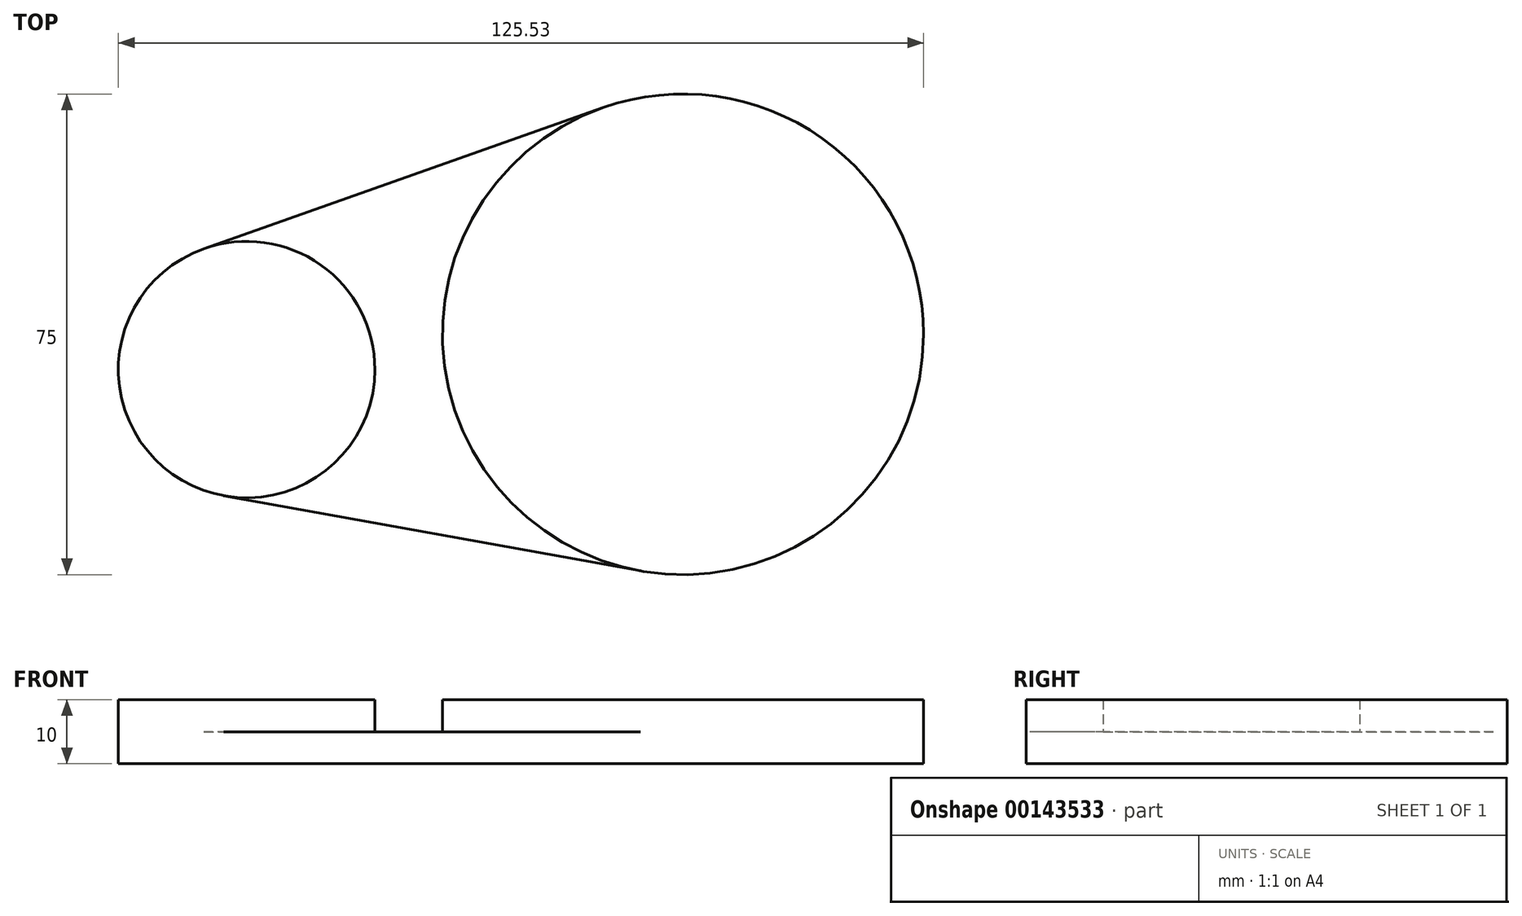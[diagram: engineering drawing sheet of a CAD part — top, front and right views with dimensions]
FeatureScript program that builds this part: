
annotation { "Feature Type Name" : "Feature", "Feature Type Description" : "" }
export const myFeature = defineFeature(function(context is Context, id is Id, definition is map)
    precondition{}
    {
        {
            var Q0;
            Q0=qCreatedBy(makeId("Top.planeOp"),FACE);
            var sketch = newSketch(context, id + "F0", { "sketchPlane" : qUnion([Q0])});
            skCircle(sketch, "E0", {"center": v(-39.37, 5.77) * mm, "radius": 20 * mm});
            skCircle(sketch, "E1", {"center": v(28.66, 11.26) * mm, "radius": 37.5 * mm});
            skLineSegment(sketch, "E2", {"start": v(-46.04, 24.62) * mm, "end": v(16.16, 46.62) * mm});
            skLineSegment(sketch, "E3", {"start": v(-42.93, -13.91) * mm, "end": v(22, -25.64) * mm});
            skLineSegment(sketch, "E4.bottom", {"start": v(-58.75, -32.63) * mm, "end": v(-24.57, -32.63) * mm});
            skLineSegment(sketch, "E4.top", {"start": v(-58.75, -59.6) * mm, "end": v(-24.57, -59.6) * mm});
            skLineSegment(sketch, "E4.left", {"start": v(-58.75, -32.63) * mm, "end": v(-58.75, -59.6) * mm});
            skLineSegment(sketch, "E4.right", {"start": v(-24.57, -32.63) * mm, "end": v(-24.57, -59.6) * mm});
            skCircle(sketch, "E5.cCircle", {"center": v(-42.22, -37.82) * mm, "radius": 5.19 * mm, "construction": true});
            skLineSegment(sketch, "E5.0", {"start": v(-45.21, -32.63) * mm, "end": v(-39.22, -32.63) * mm});
            skLineSegment(sketch, "E5.1", {"start": v(-39.22, -32.63) * mm, "end": v(-36.22, -37.82) * mm});
            skLineSegment(sketch, "E5.2", {"start": v(-36.22, -37.82) * mm, "end": v(-39.22, -43) * mm});
            skLineSegment(sketch, "E5.3", {"start": v(-39.22, -43) * mm, "end": v(-45.21, -43) * mm});
            skLineSegment(sketch, "E5.4", {"start": v(-45.21, -43) * mm, "end": v(-48.2, -37.82) * mm});
            skLineSegment(sketch, "E5.5", {"start": v(-48.2, -37.82) * mm, "end": v(-45.21, -32.63) * mm});
            skPoint(sketch, "E5.0.midPoint", {"position": v(-42.22, -32.63) * mm});
            skCircle(sketch, "E6.cCircle", {"center": v(-53.03, -35.72) * mm, "radius": 2 * mm, "construction": true});
            skLineSegment(sketch, "E6.0", {"start": v(-51.87, -37.72) * mm, "end": v(-54.18, -37.72) * mm});
            skLineSegment(sketch, "E6.1", {"start": v(-54.18, -37.72) * mm, "end": v(-55.34, -35.72) * mm});
            skLineSegment(sketch, "E6.2", {"start": v(-55.34, -35.72) * mm, "end": v(-54.18, -33.72) * mm});
            skLineSegment(sketch, "E6.3", {"start": v(-54.18, -33.72) * mm, "end": v(-51.87, -33.72) * mm});
            skLineSegment(sketch, "E6.4", {"start": v(-51.87, -33.72) * mm, "end": v(-50.72, -35.72) * mm});
            skLineSegment(sketch, "E6.5", {"start": v(-50.72, -35.72) * mm, "end": v(-51.87, -37.72) * mm});
            skPoint(sketch, "E6.0.midPoint", {"position": v(-53.03, -37.72) * mm});
            skCircle(sketch, "E7", {"center": v(-6.19, -55.66) * mm, "radius": 15.94 * mm});
            skCircle(sketch, "E8.cCircle", {"center": v(-12.82, -45.74) * mm, "radius": 2.54 * mm, "construction": true});
            skLineSegment(sketch, "E8.0", {"start": v(-9.92, -45.34) * mm, "end": v(-11.02, -48.05) * mm});
            skLineSegment(sketch, "E8.1", {"start": v(-11.02, -48.05) * mm, "end": v(-13.93, -48.45) * mm});
            skLineSegment(sketch, "E8.2", {"start": v(-13.93, -48.45) * mm, "end": v(-15.73, -46.14) * mm});
            skLineSegment(sketch, "E8.3", {"start": v(-15.73, -46.14) * mm, "end": v(-14.62, -43.42) * mm});
            skLineSegment(sketch, "E8.4", {"start": v(-14.62, -43.42) * mm, "end": v(-11.72, -43.02) * mm});
            skLineSegment(sketch, "E8.5", {"start": v(-11.72, -43.02) * mm, "end": v(-9.92, -45.34) * mm});
            skPoint(sketch, "E8.0.midPoint", {"position": v(-10.47, -46.7) * mm});
            skLineSegment(sketch, "E9", {"start": v(-18.63, -70.73) * mm, "end": v(-13.16, -66.48) * mm});
            skSolve(sketch);
        }
        {
            var Q0;
            {var subQ0=sQuery(id+"F0.wireOp",EDGE,"E0");var subQ1=makeQuery(id+"F0.imprint","INTERSECT",VERTEX,{"derivedFrom":[subQ0,sQuery(id+"F0.wireOp",EDGE,"E2")]});Q0=makeQuery(id+"F0.imprint","IMPRINT",FACE,{"disambiguationData":[TD([[makeQuery(id+"F0.imprint","IMPRINT",EDGE,{"disambiguationData":[TD([[subQ1,-1.0]])],"derivedFrom":subQ0}),1.0]])]});}
            var Q1;
            {var subQ0=sQuery(id+"F0.wireOp",EDGE,"E1");var subQ1=makeQuery(id+"F0.imprint","INTERSECT",VERTEX,{"derivedFrom":[subQ0,sQuery(id+"F0.wireOp",EDGE,"E2")]});Q1=makeQuery(id+"F0.imprint","IMPRINT",FACE,{"disambiguationData":[TD([[makeQuery(id+"F0.imprint","IMPRINT",EDGE,{"disambiguationData":[TD([[subQ1,-1.0]])],"derivedFrom":subQ0}),1.0]])]});}
            extrude(context, id + "F1", {"entities" : qUnion([Q0, Q1]), "depth" : 10 * mm, "offsetDistance" : 25 * mm});
        }
        {
            var Q0;
            {var subQ0=sQuery(id+"F0.wireOp",EDGE,"E2");Q0=makeQuery(id+"F0.imprint","IMPRINT",FACE,{"disambiguationData":[TD([[makeQuery(id+"F0.imprint","IMPRINT",EDGE,{"derivedFrom":subQ0}),-1.0]])]});}
            extrude(context, id + "F2", {"entities" : qUnion([Q0]), "operationType" : NewBodyOperationType.ADD, "flatOperationType" : FlatOperationType.REMOVE, "depth" : 5 * mm, "offsetDistance" : 25 * mm, "domain" : OperationDomain.MODEL});
        }
    });
